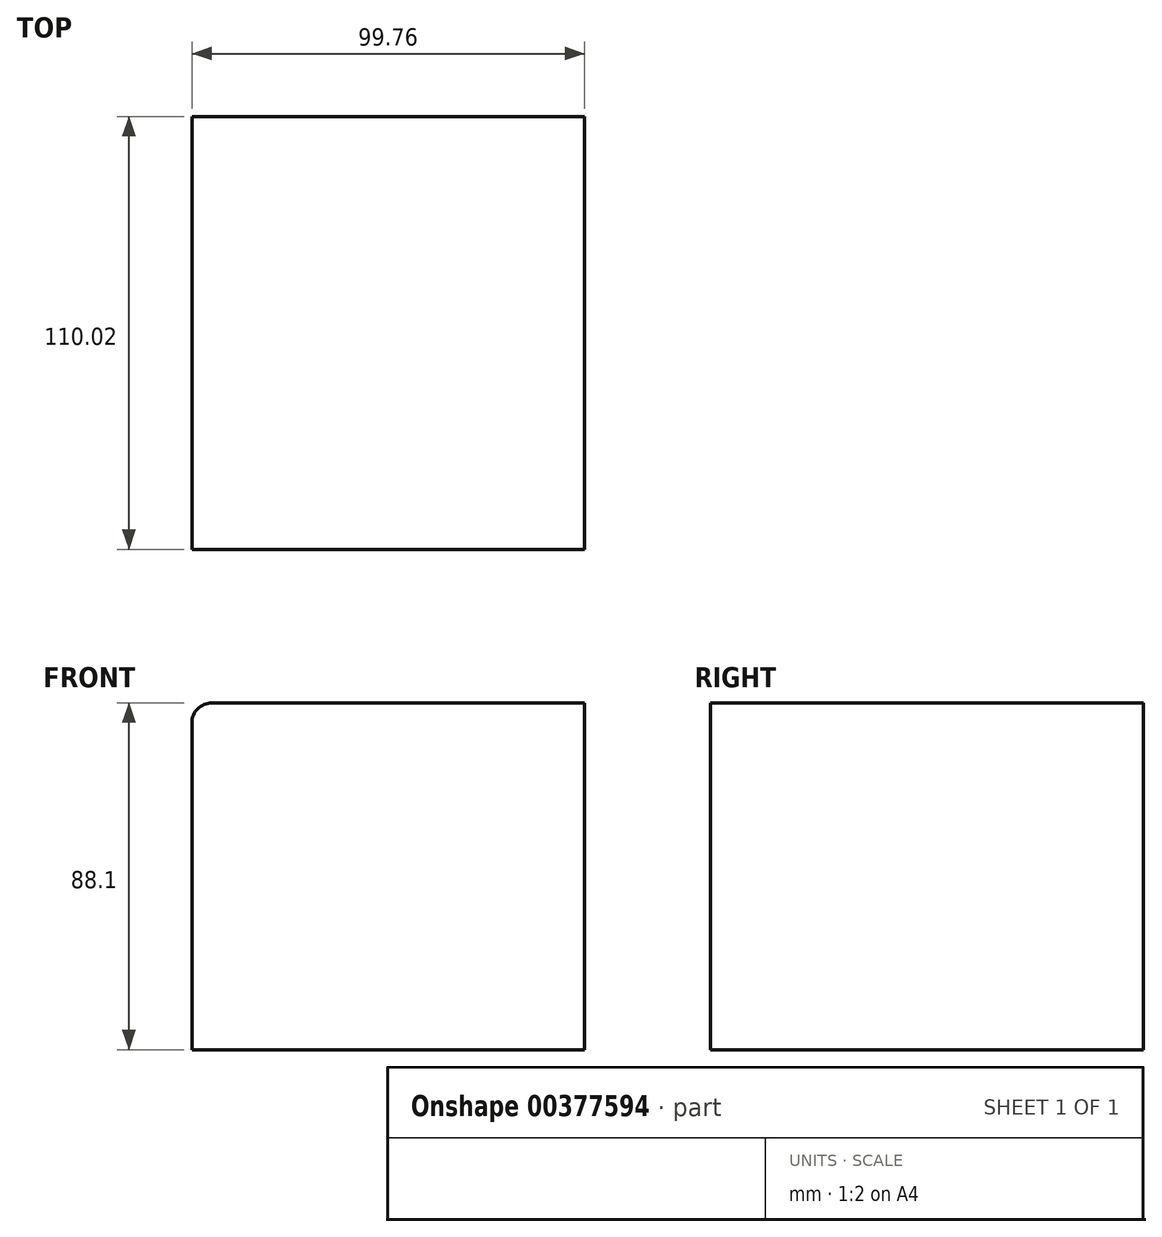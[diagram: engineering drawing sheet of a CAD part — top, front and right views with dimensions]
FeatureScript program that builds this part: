
annotation { "Feature Type Name" : "Feature", "Feature Type Description" : "" }
export const myFeature = defineFeature(function(context is Context, id is Id, definition is map)
    precondition{}
    {
        {
            var Q0;
            Q0=qCreatedBy(makeId("Front.planeOp"),FACE);
            var sketch = newSketch(context, id + "F0", { "sketchPlane" : qUnion([Q0])});
            skLineSegment(sketch, "E0.bottom", {"start": v(49.75, 42.34) * mm, "end": v(-50, 42.34) * mm});
            skLineSegment(sketch, "E0.top", {"start": v(49.75, -45.76) * mm, "end": v(-50, -45.76) * mm});
            skLineSegment(sketch, "E0.left", {"start": v(49.75, 42.34) * mm, "end": v(49.75, -45.76) * mm});
            skLineSegment(sketch, "E0.right", {"start": v(-50, 42.34) * mm, "end": v(-50, -45.76) * mm});
            skSolve(sketch);
        }
        {
            var Q0;
            Q0=makeQuery(id+"F0.imprint","IMPRINT",FACE,{"disambiguationData":[TD([[makeQuery(id+"F0.imprint","IMPRINT",EDGE,{"derivedFrom":sQuery(id+"F0.wireOp",EDGE,"E0.bottom")}),1.0]])]});
            extrude(context, id + "F1", {"entities" : qUnion([Q0]), "depth" : 110.02 * mm});
        }
        {
            var Q0;
            Q0=makeQuery(id+"F1.opExtrude","SWEPT_EDGE",EDGE,{"disambiguationData":[OSD([sQuery(id+"F0.wireOp",EDGE,"E0.bottom"),sQuery(id+"F0.wireOp",EDGE,"E0.right")])]});
            fillet(context, id + "F2", {"entities" : qUnion([Q0]), "radius" : 5.08 * mm, "tangentPropagation" : true, "allowEdgeOverflow" : false});
        }
    });
